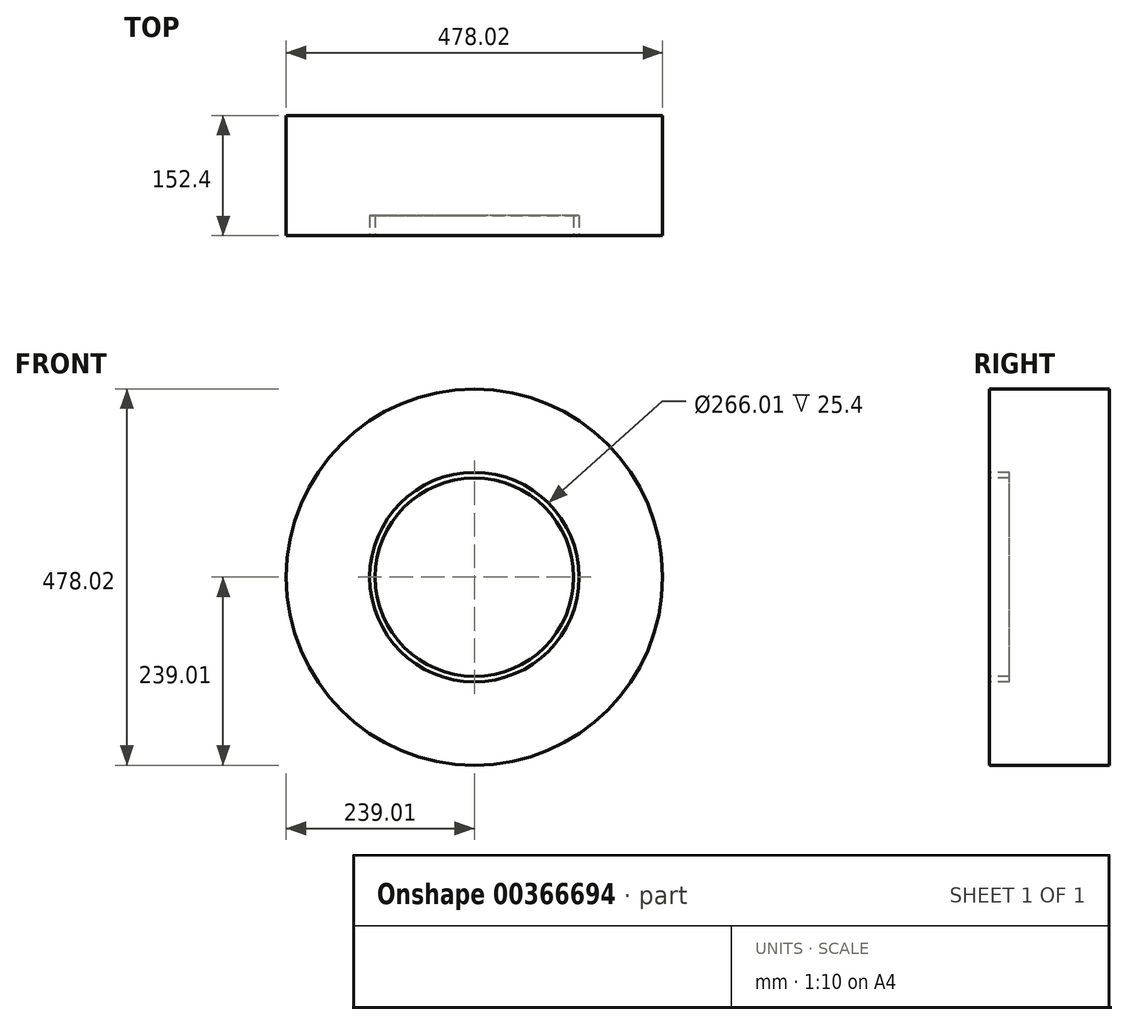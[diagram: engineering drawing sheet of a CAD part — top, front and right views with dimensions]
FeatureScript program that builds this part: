
annotation { "Feature Type Name" : "Feature", "Feature Type Description" : "" }
export const myFeature = defineFeature(function(context is Context, id is Id, definition is map)
    precondition{}
    {
        {
            var Q0;
            Q0=qCreatedBy(makeId("Front.planeOp"),FACE);
            var sketch = newSketch(context, id + "F0", { "sketchPlane" : qUnion([Q0])});
            skCircle(sketch, "E0", {"center": v(0, 0) * mm, "radius": 239.01 * mm});
            skSolve(sketch);
        }
        {
            var Q0;
            Q0 = qSketchRegion(id + "F0", true);
            extrude(context, id + "F1", {"entities" : qUnion([Q0]), "depth" : 152.4 * mm});
        }
        {
            var Q0;
            Q0=makeQuery(id+"F1.opExtrude","CAP_FACE",FACE,{"disambiguationData":[OSD([sQuery(id+"F0.wireOp",EDGE,"E0")])],"isStart":false});
            var sketch = newSketch(context, id + "F2", { "sketchPlane" : qUnion([Q0])});
            skCircle(sketch, "E1", {"center": v(0, 0) * mm, "radius": 133 * mm});
            skCircle(sketch, "E2", {"center": v(0, 0) * mm, "radius": 125.98 * mm});
            skSolve(sketch);
        }
        {
            var Q0;
            Q0 = qSketchRegion(id + "F2", true);
            extrude(context, id + "F3", {"entities" : qUnion([Q0]), "operationType" : NewBodyOperationType.REMOVE, "oppositeDirection" : true, "depth" : 25.4 * mm});
        }
    });
